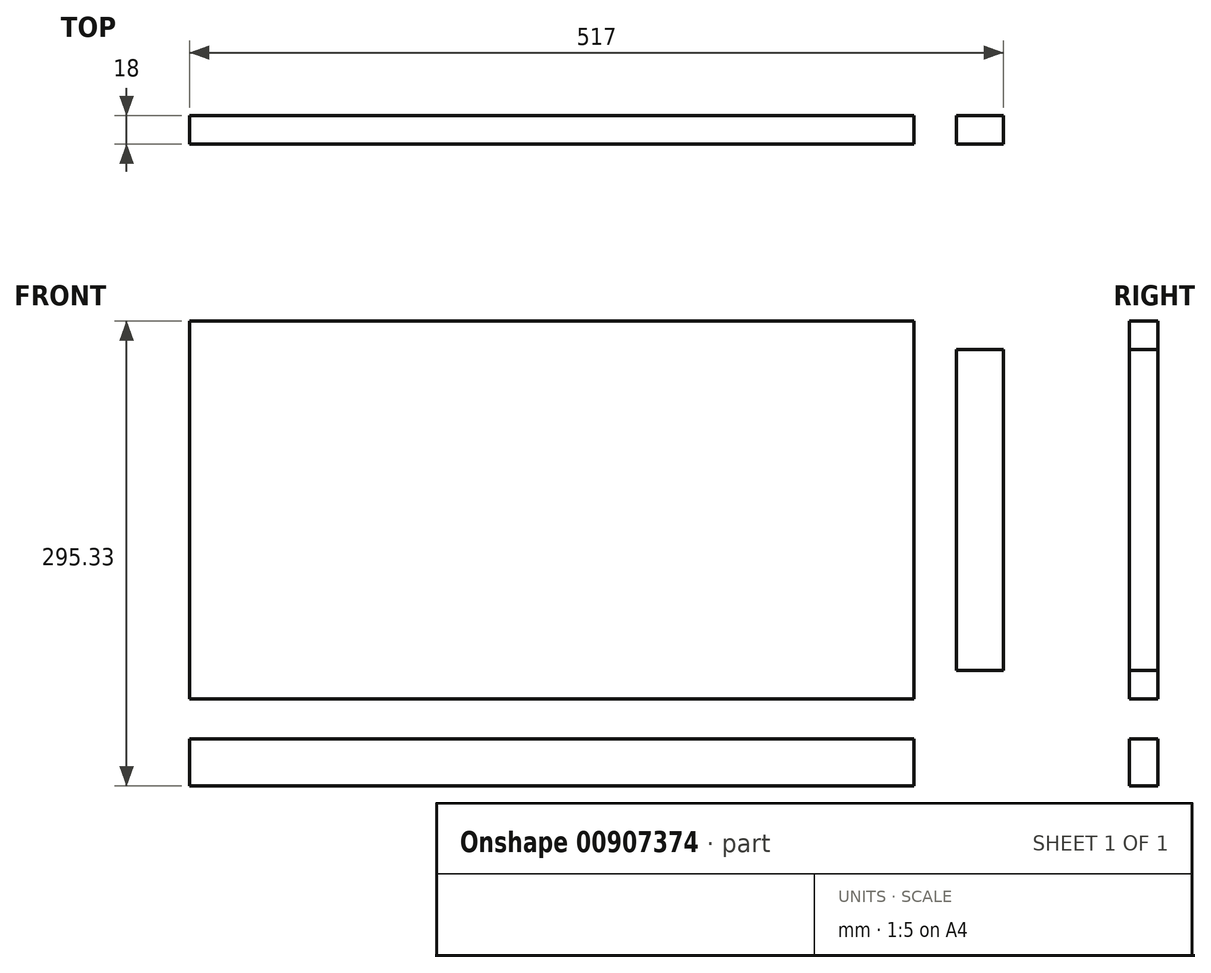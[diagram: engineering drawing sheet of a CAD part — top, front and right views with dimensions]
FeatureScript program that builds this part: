
annotation { "Feature Type Name" : "Feature", "Feature Type Description" : "" }
export const myFeature = defineFeature(function(context is Context, id is Id, definition is map)
    precondition{}
    {
        {
            var Q0;
            Q0=qCreatedBy(makeId("Front.planeOp"),FACE);
            var sketch = newSketch(context, id + "F0", { "sketchPlane" : qUnion([Q0])});
            skLineSegment(sketch, "E0.bottom", {"start": v(-225.23, -56.44) * mm, "end": v(234.77, -56.44) * mm});
            skLineSegment(sketch, "E0.top", {"start": v(-225.23, 183.56) * mm, "end": v(234.77, 183.56) * mm});
            skLineSegment(sketch, "E0.left", {"start": v(-225.23, -56.44) * mm, "end": v(-225.23, 183.56) * mm});
            skLineSegment(sketch, "E0.right", {"start": v(234.77, -56.44) * mm, "end": v(234.77, 183.56) * mm});
            skLineSegment(sketch, "E1.bottom", {"start": v(-225.23, -81.77) * mm, "end": v(234.77, -81.77) * mm});
            skLineSegment(sketch, "E1.top", {"start": v(-225.23, -111.77) * mm, "end": v(234.77, -111.77) * mm});
            skLineSegment(sketch, "E1.left", {"start": v(-225.23, -81.77) * mm, "end": v(-225.23, -111.77) * mm});
            skLineSegment(sketch, "E1.right", {"start": v(234.77, -81.77) * mm, "end": v(234.77, -111.77) * mm});
            skLineSegment(sketch, "E2.bottom", {"start": v(261.77, -38.44) * mm, "end": v(291.77, -38.44) * mm});
            skLineSegment(sketch, "E2.top", {"start": v(261.77, 165.56) * mm, "end": v(291.77, 165.56) * mm});
            skLineSegment(sketch, "E2.left", {"start": v(261.77, -38.44) * mm, "end": v(261.77, 165.56) * mm});
            skLineSegment(sketch, "E2.right", {"start": v(291.77, -38.44) * mm, "end": v(291.77, 165.56) * mm});
            skSolve(sketch);
        }
        {
            var Q0;
            Q0 = qSketchRegion(id + "F0", true);
            extrude(context, id + "F1", {"entities" : qUnion([Q0]), "depth" : 18 * mm, "offsetDistance" : 25 * mm});
        }
    });
